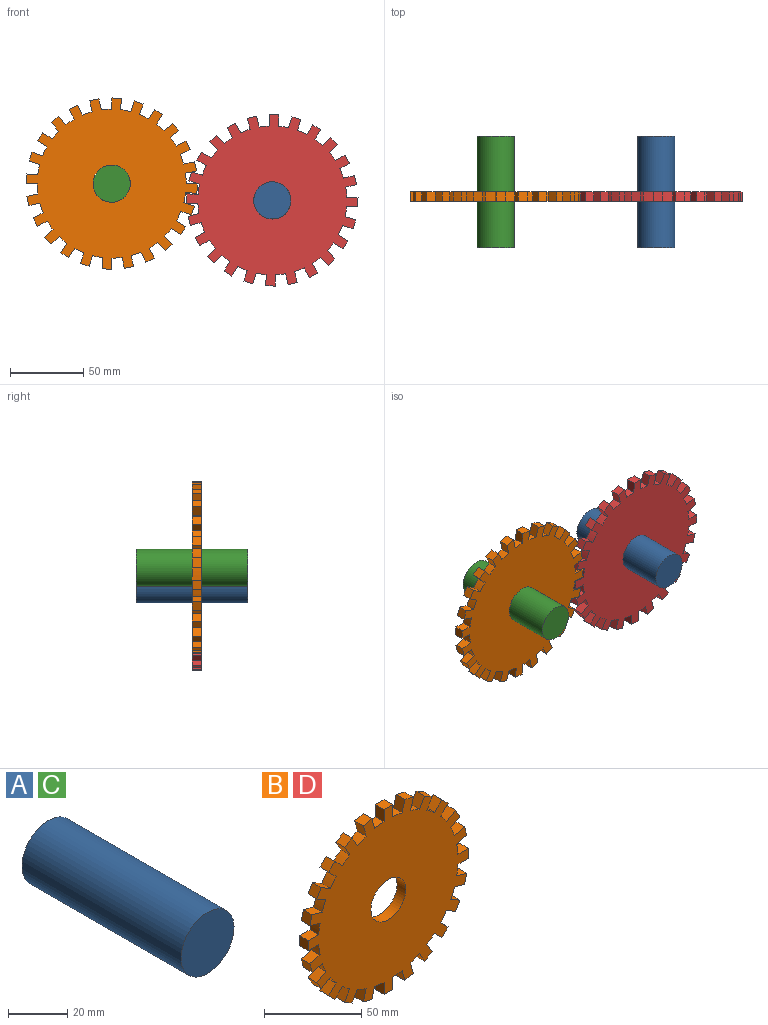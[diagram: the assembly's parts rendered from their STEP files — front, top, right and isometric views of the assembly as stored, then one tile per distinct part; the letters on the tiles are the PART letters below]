
ASSEMBLY  parts=4 mates=5
PART A: 3 faces, bbox 25.3x76.2x25.3 mm
  f0: cylinder r=12.67mm len=76.2mm, axis (0,1,0), area 6068.3mm2, adj f1,f2
  f1: plane 25.35x25.35mm, normal (0,-1,0), area 504.7mm2, adj f0
  f2: plane 25.35x25.35mm, normal (0,1,0), area 504.7mm2, adj f0
PART B: 99 faces, bbox 116.6x6.4x116.6 mm
  f0: cylinder r=50.8mm len=6.88mm, axis (0,1,0), area 44.1mm2, adj f1,f95,f96,f97
  f1: plane 7.62x6.35mm, normal (0,0,-1), area 48.4mm2, adj f0,f2,f96,f97
  f2: plane 6.35x6.35mm, normal (1,0,0), area 40.3mm2, adj f1,f3,f96,f97
  f3: plane 7.62x6.35mm, normal (0,0,1), area 48.4mm2, adj f2,f4,f96,f97
  f4: cylinder r=50.8mm len=6.88mm, axis (0,1,0), area 44.1mm2, adj f3,f5,f96,f97
  f5: plane 7.36x6.35mm, normal (0.26,0,-0.97), area 48.4mm2, adj f4,f6,f96,f97
  f6: plane 6.35x6.13mm, normal (0.97,0,0.26), area 40.3mm2, adj f5,f7,f96,f97
  f7: plane 7.36x6.35mm, normal (-0.26,0,0.97), area 48.4mm2, adj f6,f8,f96,f97
  f8: cylinder r=50.8mm len=6.41mm, axis (0,1,0), area 44.1mm2, adj f7,f9,f96,f97
  f9: plane 6.6x6.35mm, normal (0.5,0,-0.87), area 48.4mm2, adj f8,f10,f96,f97
  f10: plane 6.35x5.5mm, normal (0.87,0,0.5), area 40.3mm2, adj f9,f11,f96,f97
  f11: plane 6.6x6.35mm, normal (-0.5,0,0.87), area 48.4mm2, adj f10,f12,f96,f97
  f12: cylinder r=50.8mm len=6.35mm, axis (0,1,0), area 44.1mm2, adj f11,f13,f96,f97
  f13: plane 6.35x5.39mm, normal (0.71,0,-0.71), area 48.4mm2, adj f12,f14,f96,f97
  f14: plane 6.35x4.49mm, normal (0.71,0,0.71), area 40.3mm2, adj f13,f15,f96,f97
  f15: plane 6.35x5.39mm, normal (-0.71,0,0.71), area 48.4mm2, adj f14,f16,f96,f97
  f16: cylinder r=50.8mm len=6.35mm, axis (0,1,0), area 44.1mm2, adj f15,f17,f96,f97
  f17: plane 6.6x6.35mm, normal (0.87,0,-0.5), area 48.4mm2, adj f16,f18,f96,f97
  f18: plane 6.35x5.5mm, normal (0.5,0,0.87), area 40.3mm2, adj f17,f19,f96,f97
  f19: plane 6.6x6.35mm, normal (-0.87,0,0.5), area 48.4mm2, adj f18,f20,f96,f97
  f20: cylinder r=50.8mm len=6.41mm, axis (0,1,0), area 44.1mm2, adj f19,f21,f96,f97
  f21: plane 7.36x6.35mm, normal (0.97,0,-0.26), area 48.4mm2, adj f20,f22,f96,f97
  f22: plane 6.35x6.13mm, normal (0.26,0,0.97), area 40.3mm2, adj f21,f23,f96,f97
  f23: plane 7.36x6.35mm, normal (-0.97,0,0.26), area 48.4mm2, adj f22,f24,f96,f97
  f24: cylinder r=50.8mm len=6.88mm, axis (0,1,0), area 44.1mm2, adj f23,f25,f96,f97
  f25: plane 7.62x6.35mm, normal (1,0,0), area 48.4mm2, adj f24,f26,f96,f97
  f26: plane 6.35x6.35mm, normal (0,0,1), area 40.3mm2, adj f25,f27,f96,f97
  f27: plane 7.62x6.35mm, normal (-1,0,0), area 48.4mm2, adj f26,f28,f96,f97
  f28: cylinder r=50.8mm len=6.88mm, axis (0,1,0), area 44.1mm2, adj f27,f29,f96,f97
  f29: plane 7.36x6.35mm, normal (0.97,0,0.26), area 48.4mm2, adj f28,f30,f96,f97
  f30: plane 6.35x6.13mm, normal (-0.26,0,0.97), area 40.3mm2, adj f29,f31,f96,f97
  f31: plane 7.36x6.35mm, normal (-0.97,0,-0.26), area 48.4mm2, adj f30,f32,f96,f97
  f32: cylinder r=50.8mm len=6.41mm, axis (0,1,0), area 44.1mm2, adj f31,f33,f96,f97
  f33: plane 6.6x6.35mm, normal (0.87,0,0.5), area 48.4mm2, adj f32,f34,f96,f97
  f34: plane 6.35x5.5mm, normal (-0.5,0,0.87), area 40.3mm2, adj f33,f35,f96,f97
  f35: plane 6.6x6.35mm, normal (-0.87,0,-0.5), area 48.4mm2, adj f34,f36,f96,f97
  f36: cylinder r=50.8mm len=6.35mm, axis (0,1,0), area 44.1mm2, adj f35,f37,f96,f97
  f37: plane 6.35x5.39mm, normal (0.71,0,0.71), area 48.4mm2, adj f36,f38,f96,f97
  f38: plane 6.35x4.49mm, normal (-0.71,0,0.71), area 40.3mm2, adj f37,f39,f96,f97
  f39: plane 6.35x5.39mm, normal (-0.71,0,-0.71), area 48.4mm2, adj f38,f40,f96,f97
  f40: cylinder r=50.8mm len=6.35mm, axis (0,1,0), area 44.1mm2, adj f39,f41,f96,f97
  f41: plane 6.6x6.35mm, normal (0.5,0,0.87), area 48.4mm2, adj f40,f42,f96,f97
  f42: plane 6.35x5.5mm, normal (-0.87,0,0.5), area 40.3mm2, adj f41,f43,f96,f97
  f43: plane 6.6x6.35mm, normal (-0.5,0,-0.87), area 48.4mm2, adj f42,f44,f96,f97
  f44: cylinder r=50.8mm len=6.41mm, axis (0,1,0), area 44.1mm2, adj f43,f45,f96,f97
  f45: plane 7.36x6.35mm, normal (0.26,0,0.97), area 48.4mm2, adj f44,f46,f96,f97
  f46: plane 6.35x6.13mm, normal (-0.97,0,0.26), area 40.3mm2, adj f45,f47,f96,f97
  f47: plane 7.36x6.35mm, normal (-0.26,0,-0.97), area 48.4mm2, adj f46,f48,f96,f97
  f48: cylinder r=50.8mm len=6.88mm, axis (0,1,0), area 44.1mm2, adj f47,f49,f96,f97
  f49: plane 7.62x6.35mm, normal (0,0,1), area 48.4mm2, adj f48,f50,f96,f97
  f50: plane 6.35x6.35mm, normal (-1,0,0), area 40.3mm2, adj f49,f51,f96,f97
  f51: plane 7.62x6.35mm, normal (0,0,-1), area 48.4mm2, adj f50,f52,f96,f97
  f52: cylinder r=50.8mm len=6.88mm, axis (0,1,0), area 44.1mm2, adj f51,f53,f96,f97
  f53: plane 7.36x6.35mm, normal (-0.26,0,0.97), area 48.4mm2, adj f52,f54,f96,f97
  f54: plane 6.35x6.13mm, normal (-0.97,0,-0.26), area 40.3mm2, adj f53,f55,f96,f97
  f55: plane 7.36x6.35mm, normal (0.26,0,-0.97), area 48.4mm2, adj f54,f56,f96,f97
  f56: cylinder r=50.8mm len=6.41mm, axis (0,1,0), area 44.1mm2, adj f55,f57,f96,f97
  f57: plane 6.6x6.35mm, normal (-0.5,0,0.87), area 48.4mm2, adj f56,f58,f96,f97
  f58: plane 6.35x5.5mm, normal (-0.87,0,-0.5), area 40.3mm2, adj f57,f59,f96,f97
  f59: plane 6.6x6.35mm, normal (0.5,0,-0.87), area 48.4mm2, adj f58,f60,f96,f97
  f60: cylinder r=50.8mm len=6.35mm, axis (0,1,0), area 44.1mm2, adj f59,f61,f96,f97
  f61: plane 6.35x5.39mm, normal (-0.71,0,0.71), area 48.4mm2, adj f60,f62,f96,f97
  f62: plane 6.35x4.49mm, normal (-0.71,0,-0.71), area 40.3mm2, adj f61,f63,f96,f97
  f63: plane 6.35x5.39mm, normal (0.71,0,-0.71), area 48.4mm2, adj f62,f64,f96,f97
  f64: cylinder r=50.8mm len=6.35mm, axis (0,1,0), area 44.1mm2, adj f63,f65,f96,f97
  f65: plane 6.6x6.35mm, normal (-0.87,0,0.5), area 48.4mm2, adj f64,f66,f96,f97
  f66: plane 6.35x5.5mm, normal (-0.5,0,-0.87), area 40.3mm2, adj f65,f67,f96,f97
  f67: plane 6.6x6.35mm, normal (0.87,0,-0.5), area 48.4mm2, adj f66,f68,f96,f97
  f68: cylinder r=50.8mm len=6.41mm, axis (0,1,0), area 44.1mm2, adj f67,f69,f96,f97
  f69: plane 7.36x6.35mm, normal (-0.97,0,0.26), area 48.4mm2, adj f68,f70,f96,f97
  f70: plane 6.35x6.13mm, normal (-0.26,0,-0.97), area 40.3mm2, adj f69,f71,f96,f97
  f71: plane 7.36x6.35mm, normal (0.97,0,-0.26), area 48.4mm2, adj f70,f72,f96,f97
  f72: cylinder r=50.8mm len=6.88mm, axis (0,1,0), area 44.1mm2, adj f71,f73,f96,f97
  f73: plane 7.62x6.35mm, normal (-1,0,0), area 48.4mm2, adj f72,f74,f96,f97
  f74: plane 6.35x6.35mm, normal (0,0,-1), area 40.3mm2, adj f73,f75,f96,f97
  f75: plane 7.62x6.35mm, normal (1,0,0), area 48.4mm2, adj f74,f76,f96,f97
  f76: cylinder r=50.8mm len=6.88mm, axis (0,1,0), area 44.1mm2, adj f75,f77,f96,f97
  f77: plane 7.36x6.35mm, normal (-0.97,0,-0.26), area 48.4mm2, adj f76,f78,f96,f97
  f78: plane 6.35x6.13mm, normal (0.26,0,-0.97), area 40.3mm2, adj f77,f79,f96,f97
  f79: plane 7.36x6.35mm, normal (0.97,0,0.26), area 48.4mm2, adj f78,f80,f96,f97
  f80: cylinder r=50.8mm len=6.41mm, axis (0,1,0), area 44.1mm2, adj f79,f81,f96,f97
  f81: plane 6.6x6.35mm, normal (-0.87,0,-0.5), area 48.4mm2, adj f80,f82,f96,f97
  f82: plane 6.35x5.5mm, normal (0.5,0,-0.87), area 40.3mm2, adj f81,f83,f96,f97
  f83: plane 6.6x6.35mm, normal (0.87,0,0.5), area 48.4mm2, adj f82,f84,f96,f97
  f84: cylinder r=50.8mm len=6.35mm, axis (0,1,0), area 44.1mm2, adj f83,f85,f96,f97
  f85: plane 6.35x5.39mm, normal (-0.71,0,-0.71), area 48.4mm2, adj f84,f86,f96,f97
  f86: plane 6.35x4.49mm, normal (0.71,0,-0.71), area 40.3mm2, adj f85,f87,f96,f97
  f87: plane 6.35x5.39mm, normal (0.71,0,0.71), area 48.4mm2, adj f86,f88,f96,f97
  f88: cylinder r=50.8mm len=6.35mm, axis (0,1,0), area 44.1mm2, adj f87,f89,f96,f97
  f89: plane 6.6x6.35mm, normal (-0.5,0,-0.87), area 48.4mm2, adj f88,f90,f96,f97
  f90: plane 6.35x5.5mm, normal (0.87,0,-0.5), area 40.3mm2, adj f89,f91,f96,f97
  f91: plane 6.6x6.35mm, normal (0.5,0,0.87), area 48.4mm2, adj f90,f92,f96,f97
  f92: cylinder r=50.8mm len=6.41mm, axis (0,1,0), area 44.1mm2, adj f91,f93,f96,f97
  f93: plane 7.36x6.35mm, normal (-0.26,0,-0.97), area 48.4mm2, adj f92,f94,f96,f97
  f94: plane 6.35x6.13mm, normal (0.97,0,-0.26), area 40.3mm2, adj f93,f95,f96,f97
  f95: plane 7.36x6.35mm, normal (0.26,0,0.97), area 48.4mm2, adj f0,f94,f96,f97
  f96: plane 116.64x116.64mm, normal (0,-1,0), area 8751.8mm2, adj f0,f1,f2,f3,f4,f5,f6,f7
  f97: plane 116.64x116.64mm, normal (0,1,0), area 8751.8mm2, adj f0,f1,f2,f3,f4,f5,f6,f7
  f98: cylinder r=12.7mm len=25.4mm, axis (0,-1,0), area 506.7mm2, adj f96,f97
PART C: same geometry as A
PART D: same geometry as B
PLACE A rot(axis=(0,1,0),180deg) t=(0,0,0)mm
PLACE B rot(axis=(0,-1,0),116.6deg) t=(-109.5,0,11.43)mm
PLACE C rot(axis=(0,1,0),94.6deg) t=(-109.5,0,11.43)mm
PLACE D rot(axis=(0,-1,0),148.8deg) t=(0,0,0)mm
MATE parallel C.f0 <-> A.f0  axis (0,1,0) through (-109.5,38.1,11.43)mm
MATE cylindrical C.f0 <-> B.f4  axis (0,1,0) through (-109.5,0,11.43)mm
MATE cylindrical A.f0 <-> D.f4  axis (0,1,0) through (0,0,0)mm
MATE cylindrical C.f0 <-> B.f98  axis (0,1,0) through (-109.5,0,11.43)mm
MATE planar C.f0 <-> A.f0  axis (0,-1,0) through (-109.5,-38.1,11.43)mm
